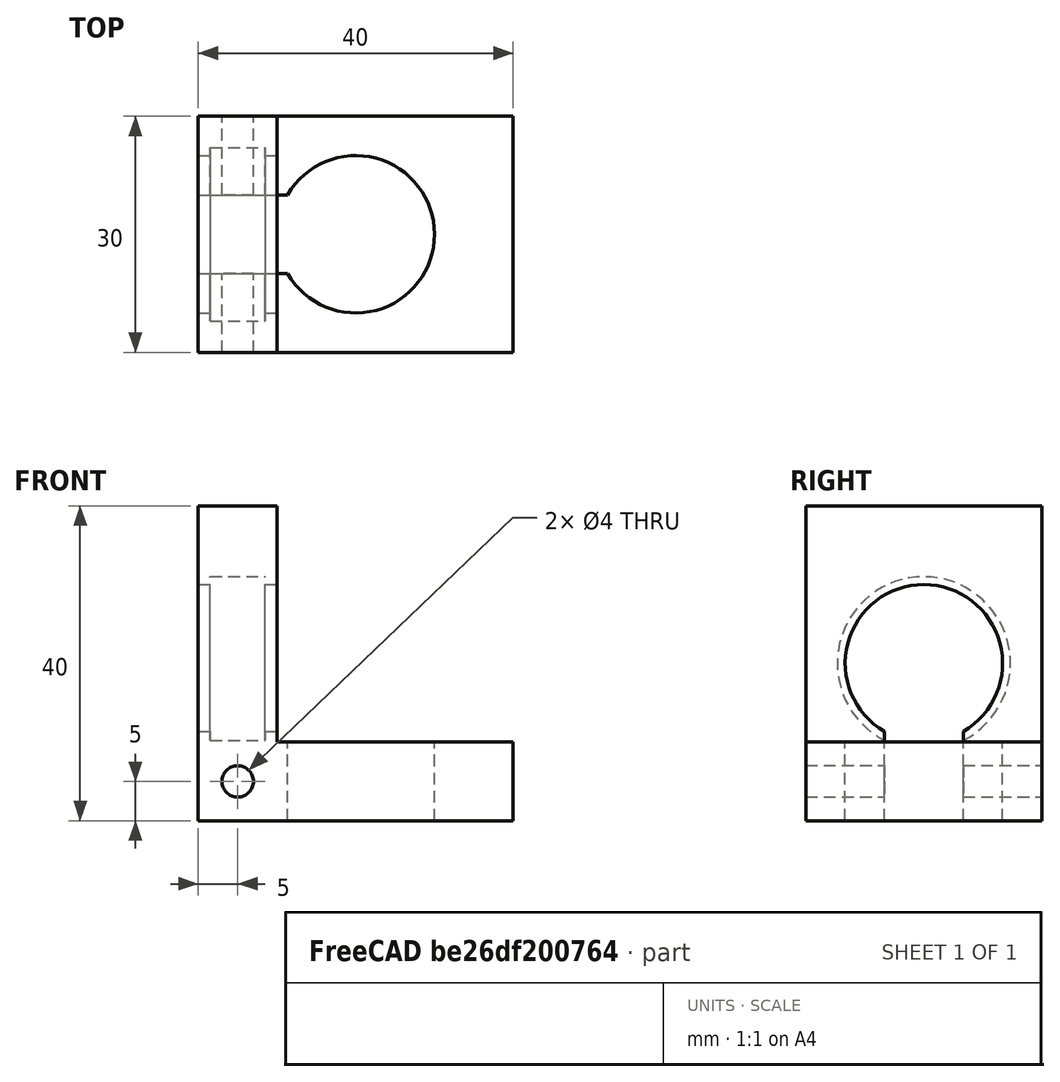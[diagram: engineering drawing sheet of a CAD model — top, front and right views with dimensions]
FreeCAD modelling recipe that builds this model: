
FCSTD DOCUMENT  (FreeCAD 0.17R13522 (Git))
Label: fastener-l-bearing
License: All rights reserved
LicenseURL: http://en.wikipedia.org/wiki/All_rights_reserved
objects: Part::Cylinder×4, Part::Box×3, Part::MultiFuse×2, Part::Cut×1
note: 10 computed .brp shape members not serialized (recipe doc carries the construction recipe); baked Part::Feature solids carry a one-line shape summary decoded from their .brp

FEATURE [Part::Cylinder] Cylinder001
  Angle = 360
  AttacherType = Attacher::AttachEngine3D
  Height = 30
  Placement = pos=(-15,-15,0) rot=(-1,0,0;1.5708rad)
  Radius = 2
FEATURE [Part::Box] Box  label="Cube"
  AttacherType = Attacher::AttachEngine3D
  Height = 10
  Length = 40
  Placement = pos=(-20,-15,-5) rot=(0,0,1;0rad)
  Width = 30
FEATURE [Part::Cylinder] Cylinder
  Angle = 360
  AttacherType = Attacher::AttachEngine3D
  Height = 10
  Placement = pos=(0,0,-5) rot=(0,0,1;0rad)
  Radius = 10
FEATURE [Part::Box] Box001  label="Cube001"
  AttacherType = Attacher::AttachEngine3D
  Height = 15
  Length = 15
  Placement = pos=(-20,-5,-5) rot=(0,0,1;0rad)
  Width = 10
FEATURE [Part::Box] Box002  label="Cube002"
  AttacherType = Attacher::AttachEngine3D
  Height = 40
  Length = 10
  Placement = pos=(-20,-15,-5) rot=(0,0,1;0rad)
  Width = 30
FEATURE [Part::Cylinder] Cylinder002  label="Bearing Cylinder"
  Angle = 360
  AttacherType = Attacher::AttachEngine3D
  Height = 7
  Placement = pos=(-18.5,0,15) rot=(0,1,0;1.5708rad)
  Radius = 11
FEATURE [Part::MultiFuse] Fusion001  label="Positive Fusion"
  Shapes = -> [Box,Box002]
FEATURE [Part::Cylinder] Cylinder003  label="Bearing Cylinder Outer"
  Angle = 360
  AttacherType = Attacher::AttachEngine3D
  Height = 10
  Placement = pos=(-20,0,15) rot=(0,1,0;1.5708rad)
  Radius = 10
FEATURE [Part::MultiFuse] Fusion  label="Negative Fusion"
  Shapes = -> [Box001,Cylinder,Cylinder001,Cylinder002,Cylinder003]
FEATURE [Part::Cut] Cut
  Base = -> Fusion001
  Tool = -> Fusion
